AUTODESK INVENTOR PART (.ipt)
format: ipt  version: 2018 (Build 220112000, 112)  size: 513,536 bytes
history: native  units: in
note: dims shown in document units (in); Inventor stores cm internally (conversion verified against a paired STEP export)
features: sketch x6, extrude x3, other x3, helix x1, plane x1
ambient origin geometry x8: Origin, YZ Plane, XZ Plane, XY Plane, X Axis, Y Axis, Z Axis, Center Point
bodies: Solid1 (feature_tree), Solid4 (feature_tree)
feature tree (14):
  extrude  "Extrusion1"  Depth=4724.4094in
  helix  "Coil2"  [1 undecoded]
  extrude  "Extrusion2"  Depth=157.4803in
  sketch  "Sketch4"  dims[d25=137.7953in d26=0.0in]
  other  "Form3"
  extrude  "Extrusion3"  [1 undecoded]
  plane  "Work Plane1"
  sketch  "Sketch8"
  sketch  "Sketch1"  dims[d0=196.8504in d1=4724.4094in d2=-0.0034in]
  sketch  "Sketch2"  dims[d11=196.8504in d12=4685.0394in d13=0.3937in d14=-0.0041in d15=90.0deg d16=90.0deg d17=0.0in d18=0.0in d19=19.685in]
  sketch  "Sketch3"  dims[d20=4953.0344in d21=190.2047in d22=0.0in d23=0.0in d24=157.4803in]
  sketch  "Sketch5"
  other  "Assembly1"
  other  "base rotor:1"
note: 2 required parameter values undecoded (feature->parameter linkage not recoverable at this tier; creation-order binding heuristic only, values carry confidence <= 0.55)
